# Revit family: i-Vent 500-1500E
name_source: partatom
category: Оборудование
revit_build: Autodesk Revit 2017 (Build: 20170118_1100(x64)
units: mm (PartAtom-declared; Revit-internal decimal feet)

## family parameters
Всегда вертикально = Да
На основе рабочей плоскости = Нет
Общий = Нет
При загрузке вырезать с полостями = Нет
Размер круглого соединителя = Использовать диаметр
Тип детали = Нормальный
Точка расчета площади = Нет

## types (3) — shared parameters
URL = https://turkov.ru
d = 20 мм
Изготовитель = Turkov
Нагреватель 12 кВт = Нагреватель : 12 кВт (380В)
Нагреватель 18 кВт = Нагреватель : 18 кВт (380В)
Нагреватель 21 кВт = Нагреватель : 21 кВт (380В)
Нагреватель 24 кВт = Нагреватель : 24 кВт (380В)
Нагреватель 27 кВт = Нагреватель : 27 кВт (380В)
Нагреватель 30 кВт = Нагреватель : 30 кВт (380В)
Нагреватель 36000 Вт = Нагреватель : 36 кВт (380В)
Нагреватель 4500 Вт = Нагреватель : 4.5 кВт (220В)
Нагреватель 4500 Вт 380в = Нагреватель : 4.5 кВт (380В)
Нагреватель 6 кВт = Нагреватель : 6.0 кВт (380В)
Нагреватель 7500 Вт = Нагреватель : 7.5 кВт (380В)
Нагреватель 9 кВт = Нагреватель : 9 кВт (380В)

## per-type parameters (varying)
| type | DN | Нагреватель 15 кВт |
| i-Vent 500E | 200 мм | Нагреватель : 18 кВт (380В) |
| i-Vent 1000E | 250 мм | Нагреватель : 15 кВт (380В) |
| i-Vent 1500E | 315 мм | Нагреватель : 15 кВт (380В) |
